# Revit family: Tiroir modulaire
name_source: partatom
category: Installations électriques
units: mm (PartAtom-declared; Revit-internal decimal feet)

## family parameters
Basée sur le plan de construction = Non
Conserver l'orientation des annotations = Non
Cote de connecteur circulaire = Utiliser le diamètre
Couper avec des vides une fois chargée = Non
Partagée = Non
Point de calcul de pièce = Non
Toujours verticalement = Oui
Type d'élément = Normal

## types (1)
- Panneau modulaire 1U à équiper
    Adapté au nombre de cassettes = 4
    Adapté au nombre de fibres = 96
    Avec boîtier = Oui
    Avec façade = Non
    Avec pigtails = Non
    Avec porte-étiquette = Oui
    Classe ETIM = EC001130
    Couleur = IDS_NOIR
    EAN = 3414970961617
    Elévation par défaut = 0 mm  [stored 0 ft]
    Fonction = Panneaux fibre optique HD 19 pouces à équiper
    Hauteur = 44 mm  [stored 0.144357 ft]
    IK = IK04
    Largeur (mm) = 483 mm
    Libellé BIM = Panneau modulaire 1U à équiper
    Lien e-catalogue = https://www.legrand.fr
    Mode de pose = Encastrement 19 pouces
    Nombre d'unités = 1
    Profondeur = 334 mm
    RAL = 9017
    Référence Legrand = 032100
    Température de fonctionnement = -10°C à 60°C
    Température de stockage = -10°C à 60°C

note: [stored X ft] marks values corroborated as IEEE doubles in the binary element streams (Revit-internal decimal feet)
